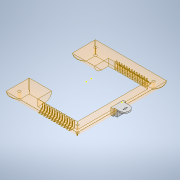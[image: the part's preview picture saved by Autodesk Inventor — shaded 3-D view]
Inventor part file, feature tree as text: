
AUTODESK INVENTOR PART (.ipt)
format: ipt  version: 2020 (Build 240168000, 168)  size: 1,234,432 bytes
history: native  units: mm
features: sketch x8, other x4, extrude x4, plane x1, fillet x1
ambient origin geometry x8: Origin, YZ Plane, XZ Plane, XY Plane, X Axis, Y Axis, Z Axis, Center Point
bodies: Body1 (feature_tree), Body2 (feature_tree)
feature tree (18):
  other  "casing-backing.ipt"
  plane  "Work Plane1"
  extrude  "Extrusion4"  Depth=10.0mm TaperAngle=0.0deg
  sketch  "Sketch9"  dims[d34=0.2mm d35=0.1mm]
  sketch  "Sketch11"  dims[d36=0.1mm d37=0.0mm d45=6.35mm]
  extrude  "Extrusion7"  Depth=0.1mm
  sketch  "Sketch13"  dims[d47=3.5mm]
  extrude  "Extrusion8"  Depth=0.1mm
  extrude  "Extrusion9"  TaperAngle=0.0deg  [1 undecoded]
  fillet  "Fillet2"  Radius=6.35mm
  other  "TaggingFeature1"
  sketch  "Sketch1"  dims[d0=10.0mm d20=10.0mm d21=0.0mm]
  sketch  "Sketch4"  dims[d32=0.1mm d33=0.1mm]
  sketch  "Sketch12"  dims[d46=3.5mm]
  sketch  "Sketch14"  dims[d48=1.75mm]
  sketch  "Sketch15"  dims[d49=6.675mm d50=26.54mm d51=0.0mm d52=5.0mm d53=29.0mm d54=0.0mm d55=6.35mm d56=3.5mm d57=3.5mm d58=1.75mm d59=6.675mm d60=29.0mm d61=0.0mm d62=19.95mm d43=0.5mm d44=0.872665mm]
  other  "Solid4::casing-backing.ipt"
  other  "Srf1"
note: 1 required parameter value undecoded (feature->parameter linkage not recoverable at this tier; creation-order binding heuristic only, values carry confidence <= 0.55)
